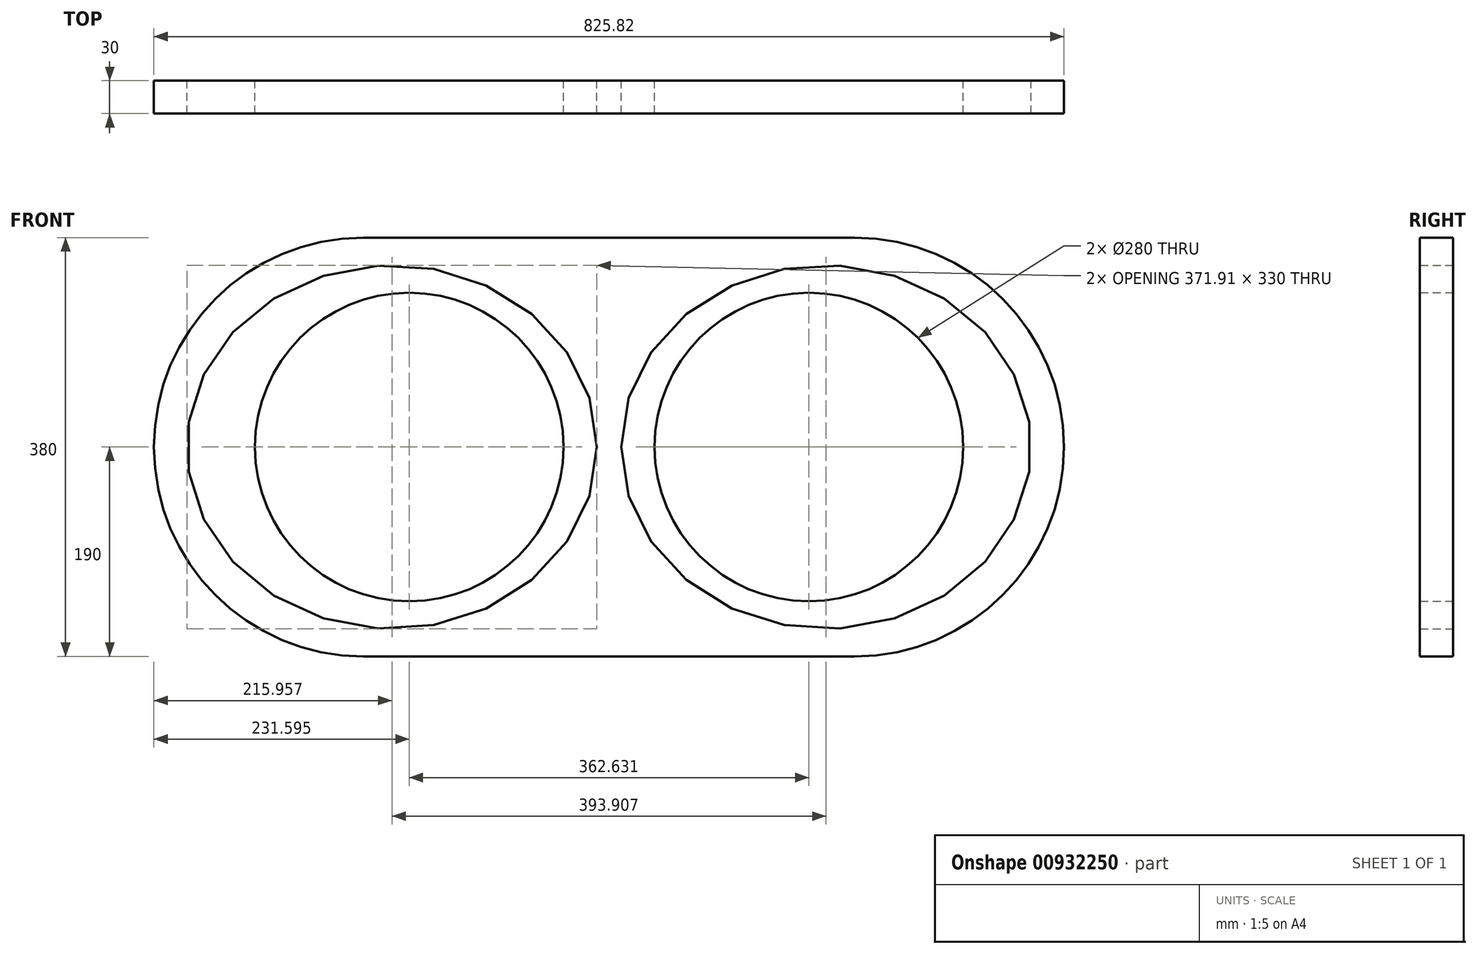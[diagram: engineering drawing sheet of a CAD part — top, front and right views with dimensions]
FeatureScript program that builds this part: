
annotation { "Feature Type Name" : "Feature", "Feature Type Description" : "" }
export const myFeature = defineFeature(function(context is Context, id is Id, definition is map)
    precondition{}
    {
        {
            var Q0;
            Q0=qCreatedBy(makeId("Front.planeOp"),FACE);
            var sketch = newSketch(context, id + "F0", { "sketchPlane" : qUnion([Q0])});
            skCircle(sketch, "E0", {"center": v(-181.32, 0) * mm, "radius": 160 * mm, "construction": true});
            skCircle(sketch, "E1.MirrorC", {"center": v(181.32, 0) * mm, "radius": 160 * mm, "construction": true});
            skEllipse(sketch, "E2", {"center": v(-196.95, 0) * mm, "majorRadius": 185.95 * mm, "minorRadius": 165 * mm, "majorAxis": v(1, 0)});
            skEllipse(sketch, "E3.MirrorC", {"center": v(196.95, 0) * mm, "majorRadius": 185.95 * mm, "minorRadius": 165 * mm, "majorAxis": v(-1, 0)});
            skLineSegment(sketch, "E4", {"start": v(0, -190) * mm, "end": v(-222.9, -190) * mm});
            skLineSegment(sketch, "E5.MirrorCS", {"start": v(0, 190) * mm, "end": v(-222.9, 190) * mm});
            skArc(sketch, "E6", {"start": v(-222.9, 190) * mm, "mid": v(-412.9, 0) * mm, "end": v(-222.9, -190) * mm});
            skLineSegment(sketch, "E7.MirrorCS", {"start": v(0, 190) * mm, "end": v(222.9, 190) * mm});
            skArc(sketch, "E8.MirrorCS", {"start": v(222.9, 190) * mm, "mid": v(412.9, 0) * mm, "end": v(222.9, -190) * mm});
            skLineSegment(sketch, "E9.MirrorCS", {"start": v(0, -190) * mm, "end": v(222.9, -190) * mm});
            skLineSegment(sketch, "E10", {"start": v(-11, 0) * mm, "end": v(11, 0) * mm, "construction": true});
            skLineSegment(sketch, "E11", {"start": v(-196.95, 165) * mm, "end": v(196.95, 165) * mm, "construction": true});
            skLineSegment(sketch, "E12", {"start": v(-412.9, 190.8) * mm, "end": v(-412.9, -168.05) * mm, "construction": true});
            skLineSegment(sketch, "E13", {"start": v(-382.9, 192.07) * mm, "end": v(-382.9, -176.96) * mm, "construction": true});
            skCircle(sketch, "E14", {"center": v(-181.32, 0) * mm, "radius": 140 * mm});
            skCircle(sketch, "E15.MirrorC", {"center": v(181.32, 0) * mm, "radius": 140 * mm});
            skSolve(sketch);
        }
        {
            var Q0;
            Q0=makeQuery(id+"F0.imprint","IMPRINT",FACE,{"disambiguationData":[TD([[makeQuery(id+"F0.imprint","IMPRINT",EDGE,{"derivedFrom":sQuery(id+"F0.wireOp",EDGE,"E2")}),-1.0]])]});
            extrude(context, id + "F1", {"entities" : qUnion([Q0]), "depth" : 30 * mm, "offsetDistance" : 25 * mm});
        }
        {
            var Q0;
            Q0=makeQuery(id+"F0.imprint","IMPRINT",FACE,{"disambiguationData":[TD([[makeQuery(id+"F0.imprint","IMPRINT",EDGE,{"derivedFrom":sQuery(id+"F0.wireOp",EDGE,"E2")}),-1.0]])]});
            var Q1;
            Q1=makeQuery(id+"F0.imprint","IMPRINT",FACE,{"disambiguationData":[TD([[makeQuery(id+"F0.imprint","IMPRINT",EDGE,{"derivedFrom":sQuery(id+"F0.wireOp",EDGE,"E2")}),1.0]])]});
            var Q2;
            Q2=makeQuery(id+"F0.imprint","IMPRINT",FACE,{"disambiguationData":[TD([[makeQuery(id+"F0.imprint","IMPRINT",EDGE,{"derivedFrom":sQuery(id+"F0.wireOp",EDGE,"E3.MirrorC")}),1.0]])]});
            extrude(context, id + "F2", {"entities" : qUnion([Q0, Q1, Q2]), "depth" : 30 * mm, "offsetDistance" : 25 * mm});
        }
    });
